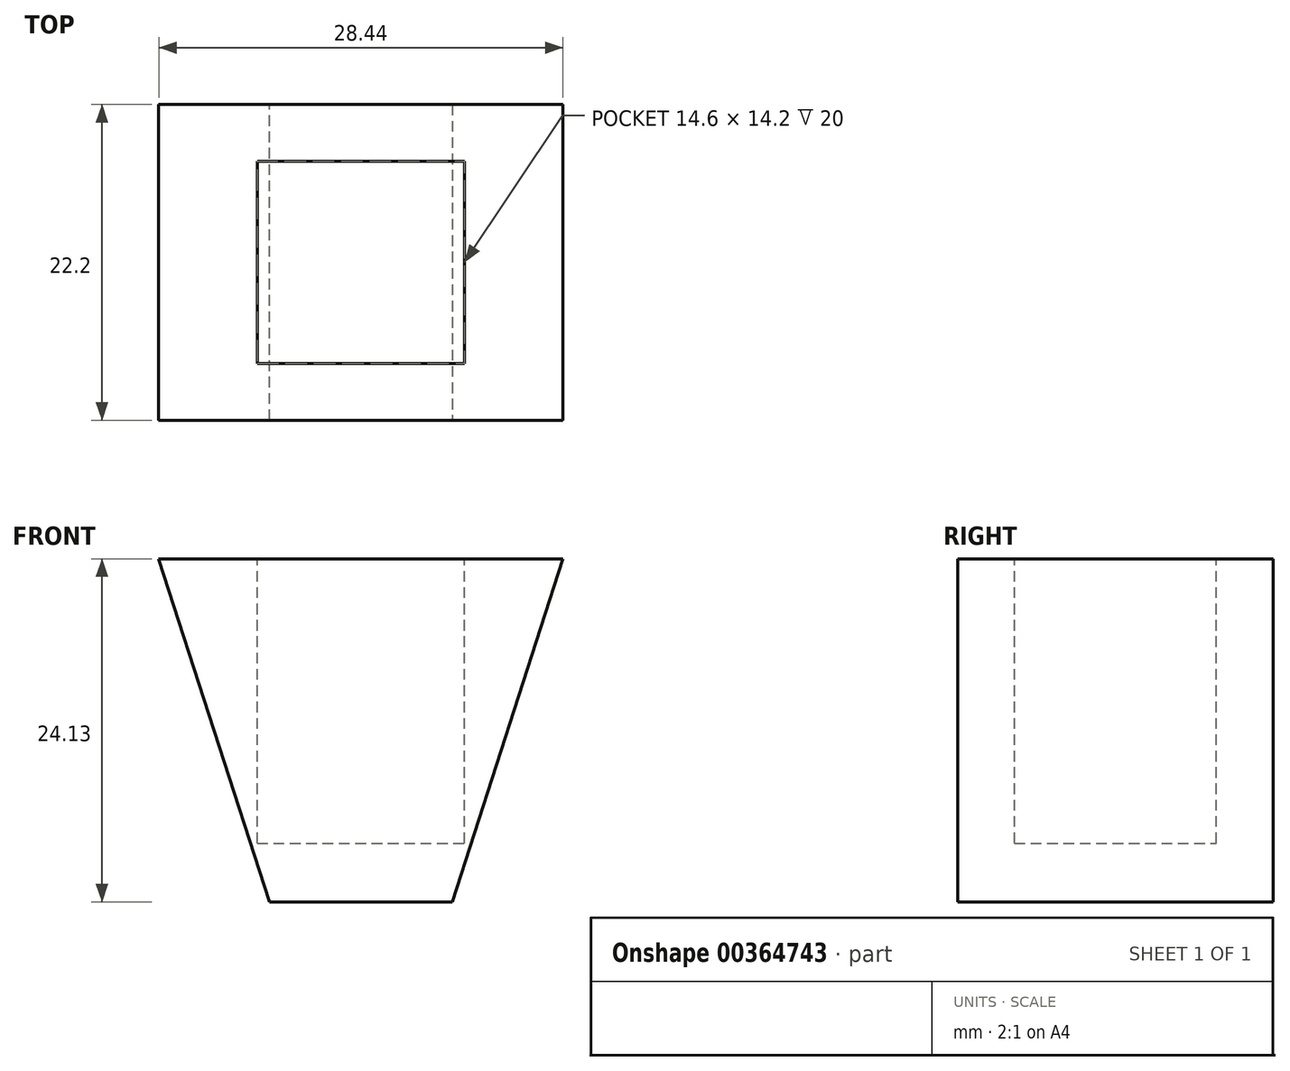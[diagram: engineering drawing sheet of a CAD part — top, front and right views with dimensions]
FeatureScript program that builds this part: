
annotation { "Feature Type Name" : "Feature", "Feature Type Description" : "" }
export const myFeature = defineFeature(function(context is Context, id is Id, definition is map)
    precondition{}
    {
        {
            var Q0;
            Q0=qCreatedBy(makeId("Top.planeOp"),FACE);
            cPlane(context, id + "F0", {"entities" : qUnion([Q0]), "cplaneType" : CPlaneType.OFFSET, "offset" : 36.12 * mm, "width" : 150 * mm, "height" : 150 * mm});
        }
        {
            var Q0;
            Q0=qCreatedBy(id+"F0.planeOp",FACE);
            var sketch = newSketch(context, id + "F1", { "sketchPlane" : qUnion([Q0])});
            skLineSegment(sketch, "E0", {"start": v(-18.1, 0) * mm, "end": v(-18.1, -22.2) * mm});
            skLineSegment(sketch, "E1", {"start": v(-18.1, -22.2) * mm, "end": v(18.1, -22.2) * mm});
            skLineSegment(sketch, "E2", {"start": v(18.1, -22.2) * mm, "end": v(18.1, 0) * mm});
            skLineSegment(sketch, "E3", {"start": v(-18.1, 0) * mm, "end": v(18.1, 0) * mm});
            skSolve(sketch);
        }
        {
            var Q0;
            Q0=qCreatedBy(makeId("Top.planeOp"),FACE);
            var sketch = newSketch(context, id + "F2", { "sketchPlane" : qUnion([Q0])});
            skLineSegment(sketch, "E4", {"start": v(6.43, 0) * mm, "end": v(6.43, -22.2) * mm});
            skLineSegment(sketch, "E5", {"start": v(6.43, -22.2) * mm, "end": v(-6.43, -22.2) * mm});
            skLineSegment(sketch, "E6", {"start": v(-6.43, -22.2) * mm, "end": v(-6.43, 0) * mm});
            skLineSegment(sketch, "E7", {"start": v(-6.43, 0) * mm, "end": v(6.43, 0) * mm});
            skSolve(sketch);
        }
        {
            var Q0;
            Q0=makeQuery(id+"F1.imprint","IMPRINT",FACE,{"disambiguationData":[TD([[makeQuery(id+"F1.imprint","IMPRINT",EDGE,{"derivedFrom":sQuery(id+"F1.wireOp",EDGE,"E0")}),1.0]])]});
            var Q1;
            Q1=makeQuery(id+"F2.imprint","IMPRINT",FACE,{"disambiguationData":[TD([[makeQuery(id+"F2.imprint","IMPRINT",EDGE,{"derivedFrom":sQuery(id+"F2.wireOp",EDGE,"E4")}),-1.0]])]});
            loft(context, id + "F3", {"sheetProfilesArray" : [{ "sheetProfileEntities" : qUnion([Q0]) }, { "sheetProfileEntities" : qUnion([Q1]) }]});
        }
        {
            var Q0;
            Q0=makeQuery(id+"F3.opLoft","CAP_FACE",FACE,{"disambiguationData":[OSD([makeQuery(id+"F1.imprint","IMPRINT",FACE,{"disambiguationData":[TD([[makeQuery(id+"F1.imprint","IMPRINT",EDGE,{"derivedFrom":sQuery(id+"F1.wireOp",EDGE,"E0")}),1.0]])]})])],"isStart":true});
            extrude(context, id + "F4", {"entities" : qUnion([Q0]), "operationType" : NewBodyOperationType.REMOVE, "oppositeDirection" : true, "depth" : 12 * mm});
        }
        {
            var Q0;
            Q0=qCreatedBy(id+"F0.planeOp",FACE);
            var sketch = newSketch(context, id + "F5", { "sketchPlane" : qUnion([Q0])});
            skLineSegment(sketch, "E8", {"start": v(-7.3, -4) * mm, "end": v(7.3, -4) * mm});
            skLineSegment(sketch, "E9", {"start": v(7.3, -4) * mm, "end": v(7.3, -18.2) * mm});
            skLineSegment(sketch, "E10", {"start": v(7.3, -18.2) * mm, "end": v(-7.3, -18.2) * mm});
            skLineSegment(sketch, "E11", {"start": v(-7.3, -18.2) * mm, "end": v(-7.3, -4) * mm});
            skSolve(sketch);
        }
        {
            var Q0;
            Q0=makeQuery(id+"F5.imprint","IMPRINT",FACE,{"disambiguationData":[TD([[makeQuery(id+"F5.imprint","IMPRINT",EDGE,{"derivedFrom":sQuery(id+"F5.wireOp",EDGE,"E8")}),-1.0]])]});
            extrude(context, id + "F6", {"entities" : qUnion([Q0]), "operationType" : NewBodyOperationType.REMOVE, "oppositeDirection" : true, "depth" : 32 * mm});
        }
    });
